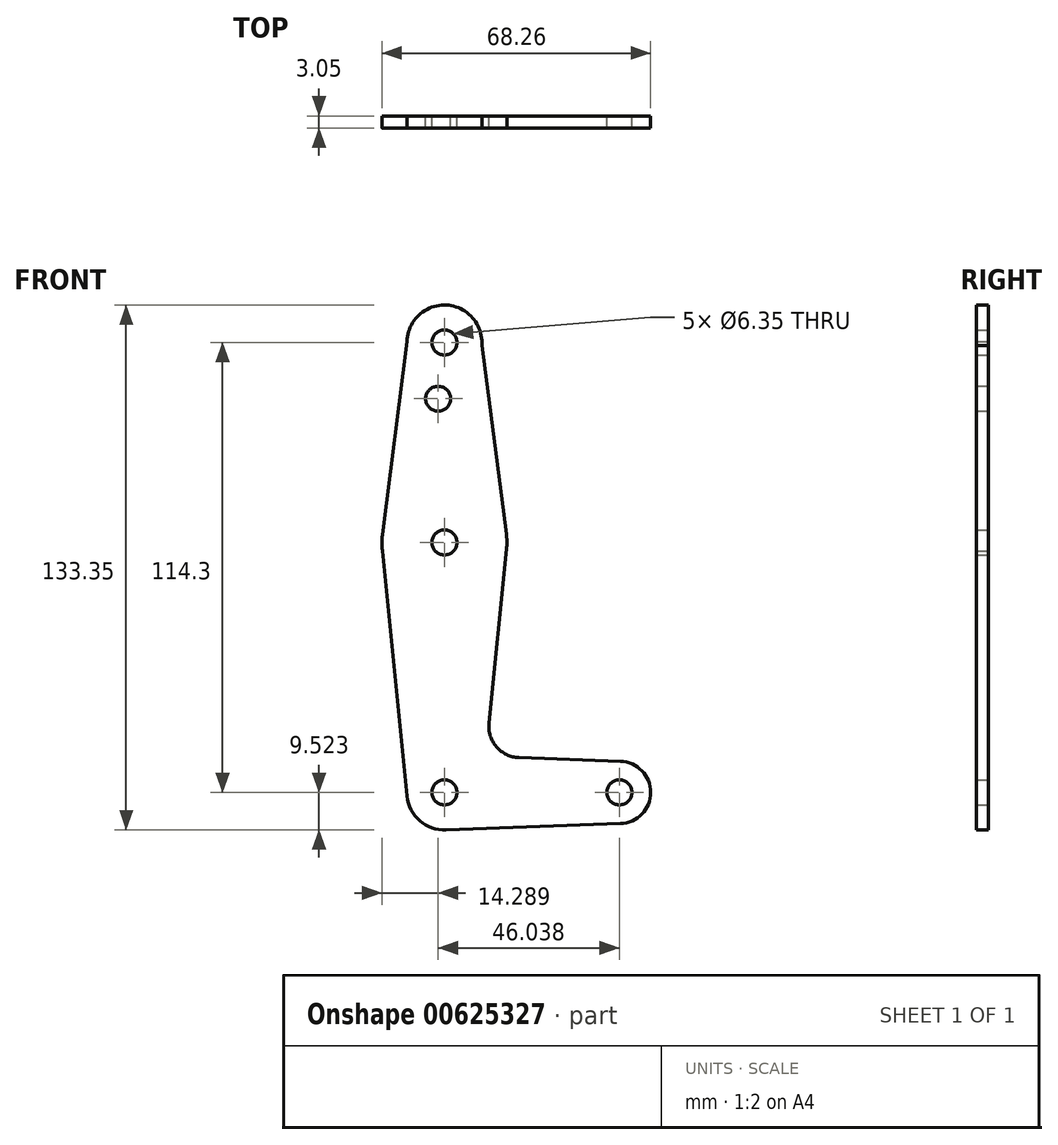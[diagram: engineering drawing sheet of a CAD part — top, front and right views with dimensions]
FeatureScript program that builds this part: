
annotation { "Feature Type Name" : "Feature", "Feature Type Description" : "" }
export const myFeature = defineFeature(function(context is Context, id is Id, definition is map)
    precondition{}
    {
        {
            var Q0;
            Q0=qCreatedBy(makeId("Front.planeOp"),FACE);
            var sketch = newSketch(context, id + "F0", { "sketchPlane" : qUnion([Q0])});
            skLineSegment(sketch, "E0", {"start": v(-32.84, 80.53) * mm, "end": v(-32.84, -33.77) * mm, "construction": true});
            skLineSegment(sketch, "E1", {"start": v(-32.84, -33.77) * mm, "end": v(11.6, -33.77) * mm, "construction": true});
            skCircle(sketch, "E2", {"center": v(-32.84, 29.73) * mm, "radius": 15.88 * mm});
            skCircle(sketch, "E3", {"center": v(-32.84, -33.77) * mm, "radius": 9.53 * mm});
            skCircle(sketch, "E4", {"center": v(-32.84, 80.53) * mm, "radius": 9.53 * mm});
            skCircle(sketch, "E5", {"center": v(11.6, -33.77) * mm, "radius": 7.94 * mm});
            skLineSegment(sketch, "E6", {"start": v(-32.84, 29.73) * mm, "end": v(-32.84, -33.77) * mm});
            skLineSegment(sketch, "E7", {"start": v(-42.37, 80.77) * mm, "end": v(-48.6, 31.73) * mm});
            skLineSegment(sketch, "E8", {"start": v(-17.1, 31.73) * mm, "end": v(-23.35, 79.79) * mm});
            skLineSegment(sketch, "E9", {"start": v(-48.58, 27.62) * mm, "end": v(-42.32, -34.72) * mm});
            skLineSegment(sketch, "E10", {"start": v(-13.9, -24.92) * mm, "end": v(11.89, -25.83) * mm});
            skLineSegment(sketch, "E11", {"start": v(-32.45, -43.28) * mm, "end": v(11.9, -41.7) * mm});
            skCircle(sketch, "E12", {"center": v(-34.43, 66.26) * mm, "radius": 3.18 * mm});
            skCircle(sketch, "E13", {"center": v(-32.84, 80.53) * mm, "radius": 3.18 * mm});
            skCircle(sketch, "E14", {"center": v(-32.84, -33.77) * mm, "radius": 3.18 * mm});
            skCircle(sketch, "E15", {"center": v(11.6, -33.77) * mm, "radius": 3.18 * mm});
            skArc(sketch, "E16.filletArc", {"start": v(-21.54, -16.17) * mm, "mid": v(-19.62, -22.2) * mm, "end": v(-13.9, -24.92) * mm});
            skLineSegment(sketch, "E17", {"start": v(-21.54, -16.17) * mm, "end": v(-17.05, 28.13) * mm});
            skCircle(sketch, "E18", {"center": v(-32.84, 29.73) * mm, "radius": 3.18 * mm});
            skSolve(sketch);
        }
        {
            var Q0;
            Q0 = qSketchRegion(id + "F0", true);
            extrude(context, id + "F1", {"entities" : qUnion([Q0]), "depth" : 3.05 * mm, "offsetDistance" : 25.4 * mm});
        }
    });
